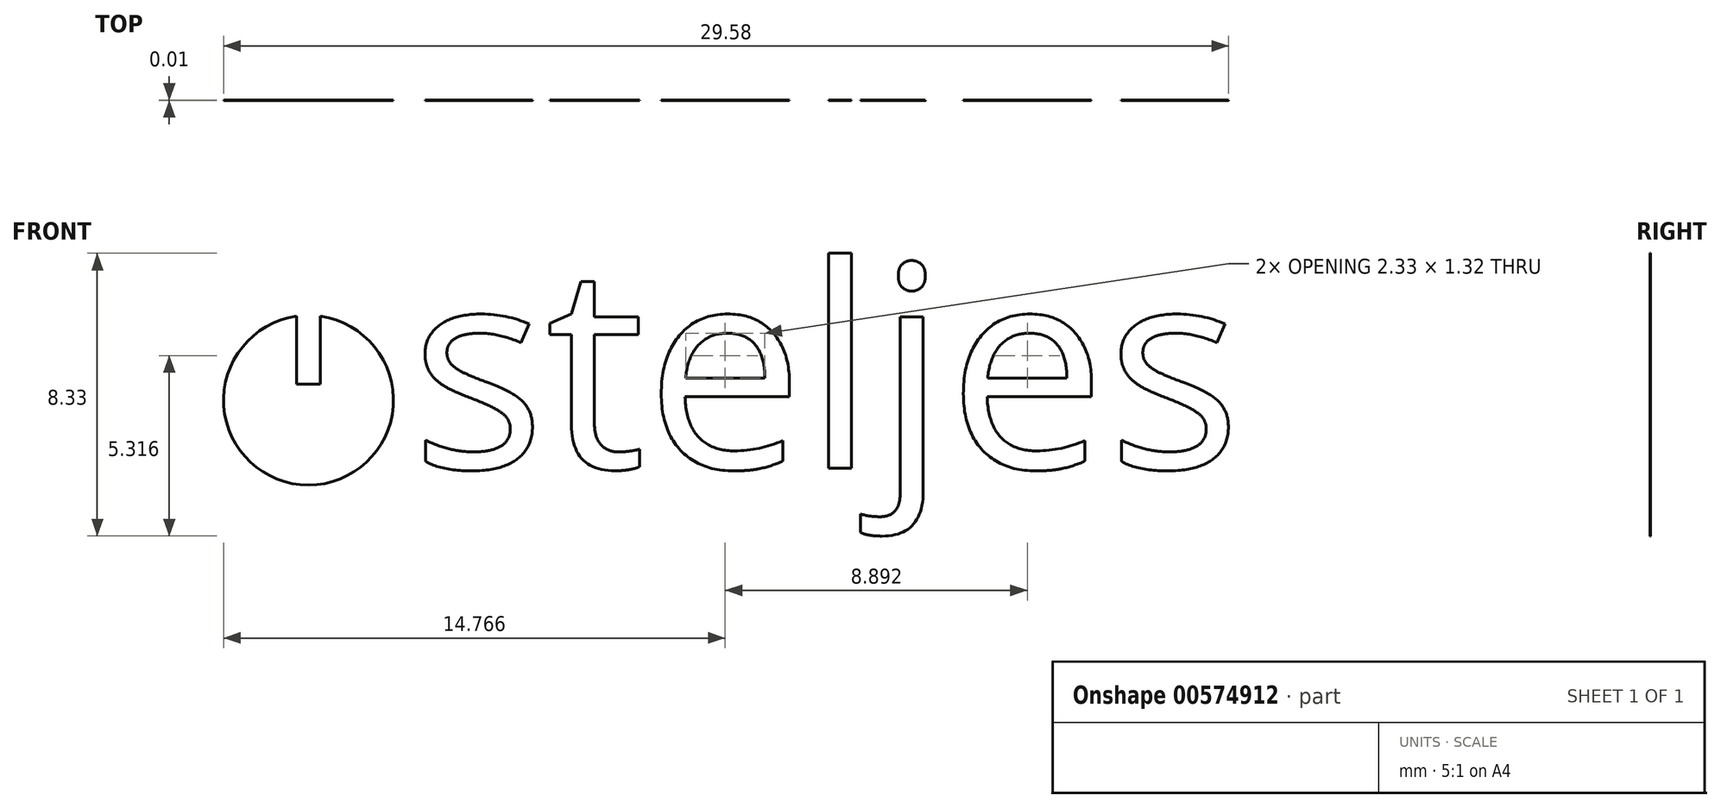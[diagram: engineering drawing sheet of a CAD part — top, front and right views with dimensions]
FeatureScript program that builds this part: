
annotation { "Feature Type Name" : "Feature", "Feature Type Description" : "" }
export const myFeature = defineFeature(function(context is Context, id is Id, definition is map)
    precondition{}
    {
        {
            var Q0;
            Q0=qCreatedBy(makeId("Front.planeOp"),FACE);
            var sketch = newSketch(context, id + "F0", { "sketchPlane" : qUnion([Q0])});
            skArc(sketch, "E0", {"start": v(-0.35, 2.48) * mm, "mid": v(0, -2.5) * mm, "end": v(0.35, 2.48) * mm});
            skLineSegment(sketch, "E1", {"start": v(-0.35, 2.48) * mm, "end": v(-0.35, 0.48) * mm});
            skLineSegment(sketch, "E2", {"start": v(-0.35, 0.48) * mm, "end": v(0.35, 0.48) * mm});
            skLineSegment(sketch, "E3", {"start": v(0.35, 0.48) * mm, "end": v(0.35, 2.48) * mm});
            skLineSegment(sketch, "E4", {"start": v(0, 0) * mm, "end": v(0, -6.2) * mm, "construction": true});
            skText(sketch, "E5", { "text": "steljes", "fontName": "OpenSans-Regular.ttf"});
            const initialGuessF0  = {"E5": [0.003, -0.002, 1, 0, 0.006]};
            skSetInitialGuess(sketch, initialGuessF0);
            skSolve(sketch);
        }
        {
            var Q0;
            Q0 = qSketchRegion(id + "F0", true);
            extrude(context, id + "F1", {"entities" : qUnion([Q0]), "depth" : 0.01 * mm, "offsetDistance" : 25 * mm});
        }
    });
